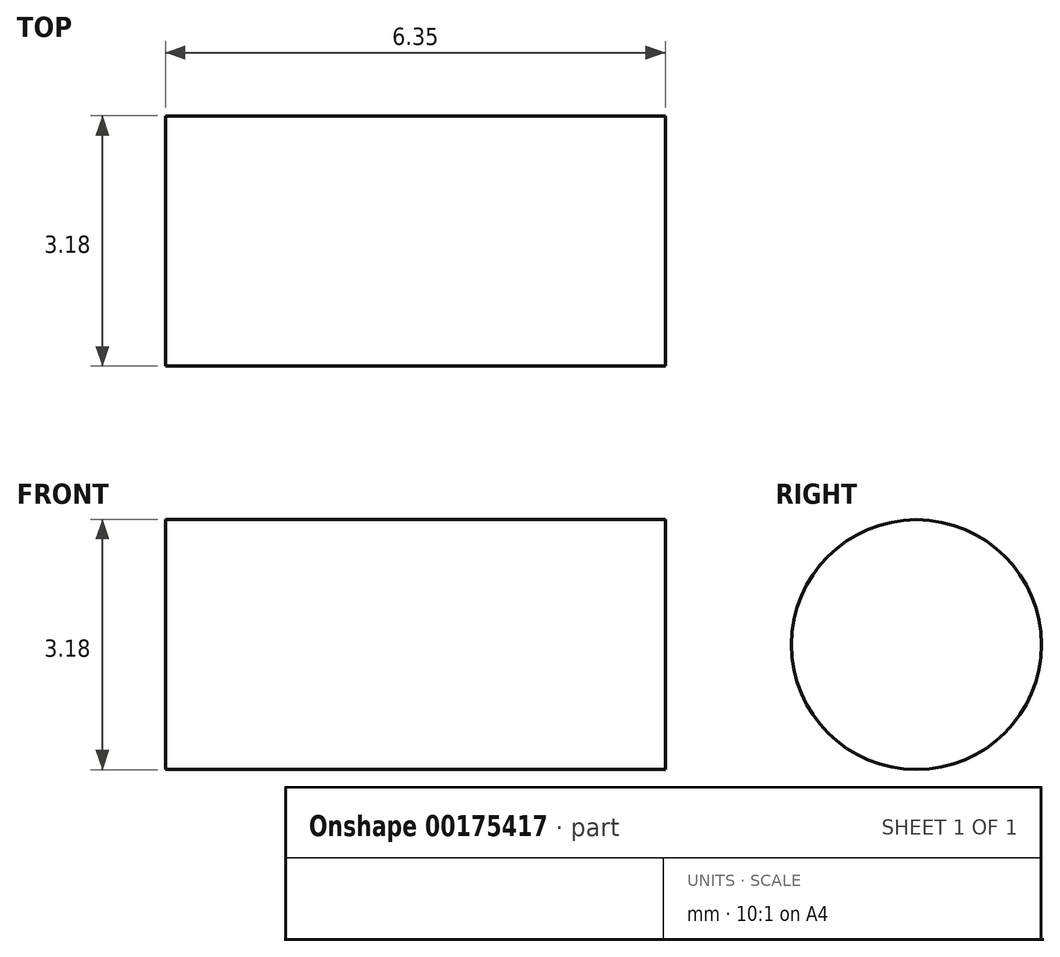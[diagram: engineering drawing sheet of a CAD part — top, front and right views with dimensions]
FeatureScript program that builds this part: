
annotation { "Feature Type Name" : "Feature", "Feature Type Description" : "" }
export const myFeature = defineFeature(function(context is Context, id is Id, definition is map)
    precondition{}
    {
        {
            var Q0;
            Q0=qCreatedBy(makeId("Right.planeOp"),FACE);
            var sketch = newSketch(context, id + "F0", { "sketchPlane" : qUnion([Q0])});
            skCircle(sketch, "E0", {"center": v(0, 0) * mm, "radius": 1.59 * mm});
            skSolve(sketch);
        }
        {
            var Q0;
            Q0=makeQuery(id+"F0.imprint","IMPRINT",FACE,{"disambiguationData":[TD([[makeQuery(id+"F0.imprint","IMPRINT",EDGE,{"derivedFrom":sQuery(id+"F0.wireOp",EDGE,"E0")}),1.0]])]});
            extrude(context, id + "F1", {"entities" : qUnion([Q0]), "depth" : 6.35 * mm});
        }
    });
